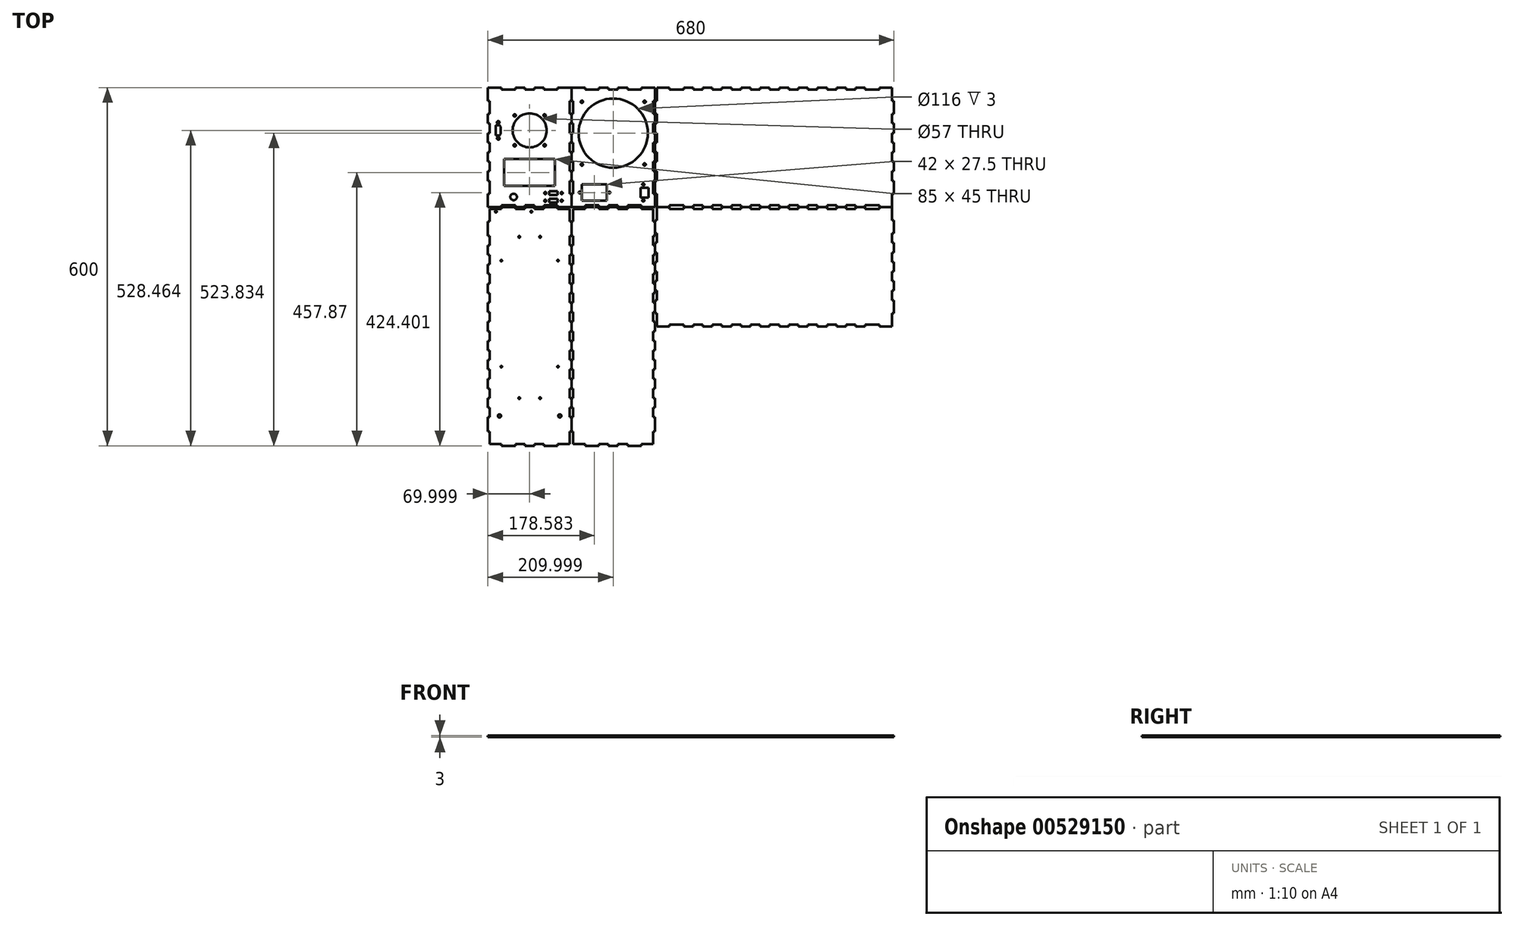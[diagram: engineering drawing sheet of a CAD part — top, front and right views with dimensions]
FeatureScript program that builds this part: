
annotation { "Feature Type Name" : "Feature", "Feature Type Description" : "" }
export const myFeature = defineFeature(function(context is Context, id is Id, definition is map)
    precondition{}
    {
        {
            var Q0;
            Q0=qCreatedBy(makeId("Top.planeOp"),FACE);
            var sketch = newSketch(context, id + "F0", { "sketchPlane" : qUnion([Q0])});
            skLineSegment(sketch, "E0", {"start": v(-340, 300) * mm, "end": v(-317, 300) * mm});
            skLineSegment(sketch, "E1", {"start": v(-317, 300) * mm, "end": v(-317, 297) * mm});
            skLineSegment(sketch, "E2", {"start": v(-317, 297) * mm, "end": v(-294, 297) * mm});
            skLineSegment(sketch, "E3", {"start": v(-294, 297) * mm, "end": v(-294, 300) * mm});
            skLineSegment(sketch, "E4", {"start": v(-294, 300) * mm, "end": v(-278, 300) * mm});
            skLineSegment(sketch, "E5", {"start": v(-278, 300) * mm, "end": v(-278, 297) * mm});
            skLineSegment(sketch, "E6", {"start": v(-278, 297) * mm, "end": v(-262, 297) * mm});
            skLineSegment(sketch, "E7", {"start": v(-262, 297) * mm, "end": v(-262, 300) * mm});
            skLineSegment(sketch, "E8", {"start": v(-262, 300) * mm, "end": v(-246, 300) * mm});
            skLineSegment(sketch, "E9", {"start": v(-246, 300) * mm, "end": v(-246, 297) * mm});
            skLineSegment(sketch, "E10", {"start": v(-246, 297) * mm, "end": v(-223, 297) * mm});
            skLineSegment(sketch, "E11", {"start": v(-223, 297) * mm, "end": v(-223, 300) * mm});
            skLineSegment(sketch, "E12", {"start": v(-223, 300) * mm, "end": v(-200, 300) * mm});
            skLineSegment(sketch, "E13", {"start": v(-200, 300) * mm, "end": v(-200, 278) * mm});
            skLineSegment(sketch, "E14", {"start": v(-200, 278) * mm, "end": v(-203, 278) * mm});
            skLineSegment(sketch, "E15", {"start": v(-203, 278) * mm, "end": v(-203, 256) * mm});
            skLineSegment(sketch, "E16", {"start": v(-203, 256) * mm, "end": v(-200, 256) * mm});
            skLineSegment(sketch, "E17", {"start": v(-200, 256) * mm, "end": v(-200, 240) * mm});
            skLineSegment(sketch, "E18", {"start": v(-200, 240) * mm, "end": v(-203, 240) * mm});
            skLineSegment(sketch, "E19", {"start": v(-203, 240) * mm, "end": v(-203, 224) * mm});
            skLineSegment(sketch, "E20", {"start": v(-203, 224) * mm, "end": v(-200, 224) * mm});
            skLineSegment(sketch, "E21", {"start": v(-200, 224) * mm, "end": v(-200, 208) * mm});
            skLineSegment(sketch, "E22", {"start": v(-200, 208) * mm, "end": v(-203, 208) * mm});
            skLineSegment(sketch, "E23", {"start": v(-203, 208) * mm, "end": v(-203, 192) * mm});
            skLineSegment(sketch, "E24", {"start": v(-203, 192) * mm, "end": v(-200, 192) * mm});
            skLineSegment(sketch, "E25", {"start": v(-200, 192) * mm, "end": v(-200, 176) * mm});
            skLineSegment(sketch, "E26", {"start": v(-200, 176) * mm, "end": v(-203, 176) * mm});
            skLineSegment(sketch, "E27", {"start": v(-203, 176) * mm, "end": v(-203, 160) * mm});
            skLineSegment(sketch, "E28", {"start": v(-203, 160) * mm, "end": v(-200, 160) * mm});
            skLineSegment(sketch, "E29", {"start": v(-200, 160) * mm, "end": v(-200, 144) * mm});
            skLineSegment(sketch, "E30", {"start": v(-200, 144) * mm, "end": v(-203, 144) * mm});
            skLineSegment(sketch, "E31", {"start": v(-203, 144) * mm, "end": v(-203, 122) * mm});
            skLineSegment(sketch, "E32", {"start": v(-203, 122) * mm, "end": v(-200, 122) * mm});
            skLineSegment(sketch, "E33", {"start": v(-200, 122) * mm, "end": v(-200, 100) * mm});
            skLineSegment(sketch, "E34", {"start": v(-200, 100) * mm, "end": v(-223, 100) * mm});
            skLineSegment(sketch, "E35", {"start": v(-223, 100) * mm, "end": v(-223, 103) * mm});
            skLineSegment(sketch, "E36", {"start": v(-223, 103) * mm, "end": v(-246, 103) * mm});
            skLineSegment(sketch, "E37", {"start": v(-246, 103) * mm, "end": v(-246, 100) * mm});
            skLineSegment(sketch, "E38", {"start": v(-246, 100) * mm, "end": v(-262, 100) * mm});
            skLineSegment(sketch, "E39", {"start": v(-262, 100) * mm, "end": v(-262, 103) * mm});
            skLineSegment(sketch, "E40", {"start": v(-262, 103) * mm, "end": v(-278, 103) * mm});
            skLineSegment(sketch, "E41", {"start": v(-278, 103) * mm, "end": v(-278, 100) * mm});
            skLineSegment(sketch, "E42", {"start": v(-278, 100) * mm, "end": v(-294, 100) * mm});
            skLineSegment(sketch, "E43", {"start": v(-294, 100) * mm, "end": v(-294, 103) * mm});
            skLineSegment(sketch, "E44", {"start": v(-294, 103) * mm, "end": v(-317, 103) * mm});
            skLineSegment(sketch, "E45", {"start": v(-317, 103) * mm, "end": v(-317, 100) * mm});
            skLineSegment(sketch, "E46", {"start": v(-317, 100) * mm, "end": v(-340, 100) * mm});
            skLineSegment(sketch, "E47", {"start": v(-340, 100) * mm, "end": v(-340, 122) * mm});
            skLineSegment(sketch, "E48", {"start": v(-340, 122) * mm, "end": v(-337, 122) * mm});
            skLineSegment(sketch, "E49", {"start": v(-337, 122) * mm, "end": v(-337, 144) * mm});
            skLineSegment(sketch, "E50", {"start": v(-337, 144) * mm, "end": v(-340, 144) * mm});
            skLineSegment(sketch, "E51", {"start": v(-340, 144) * mm, "end": v(-340, 160) * mm});
            skLineSegment(sketch, "E52", {"start": v(-340, 160) * mm, "end": v(-337, 160) * mm});
            skLineSegment(sketch, "E53", {"start": v(-337, 160) * mm, "end": v(-337, 176) * mm});
            skLineSegment(sketch, "E54", {"start": v(-337, 176) * mm, "end": v(-340, 176) * mm});
            skLineSegment(sketch, "E55", {"start": v(-340, 176) * mm, "end": v(-340, 192) * mm});
            skLineSegment(sketch, "E56", {"start": v(-340, 192) * mm, "end": v(-337, 192) * mm});
            skLineSegment(sketch, "E57", {"start": v(-337, 192) * mm, "end": v(-337, 208) * mm});
            skLineSegment(sketch, "E58", {"start": v(-337, 208) * mm, "end": v(-340, 208) * mm});
            skLineSegment(sketch, "E59", {"start": v(-340, 208) * mm, "end": v(-340, 224) * mm});
            skLineSegment(sketch, "E60", {"start": v(-340, 224) * mm, "end": v(-337, 224) * mm});
            skLineSegment(sketch, "E61", {"start": v(-337, 224) * mm, "end": v(-337, 240) * mm});
            skLineSegment(sketch, "E62", {"start": v(-337, 240) * mm, "end": v(-340, 240) * mm});
            skLineSegment(sketch, "E63", {"start": v(-340, 240) * mm, "end": v(-340, 256) * mm});
            skLineSegment(sketch, "E64", {"start": v(-340, 256) * mm, "end": v(-337, 256) * mm});
            skLineSegment(sketch, "E65", {"start": v(-337, 256) * mm, "end": v(-337, 278) * mm});
            skLineSegment(sketch, "E66", {"start": v(-337, 278) * mm, "end": v(-340, 278) * mm});
            skLineSegment(sketch, "E67", {"start": v(-340, 278) * mm, "end": v(-340, 300) * mm});
            skLineSegment(sketch, "E68", {"start": v(-200, 300) * mm, "end": v(-177, 300) * mm});
            skLineSegment(sketch, "E69", {"start": v(-177, 300) * mm, "end": v(-177, 297) * mm});
            skLineSegment(sketch, "E70", {"start": v(-177, 297) * mm, "end": v(-154, 297) * mm});
            skLineSegment(sketch, "E71", {"start": v(-154, 297) * mm, "end": v(-154, 300) * mm});
            skLineSegment(sketch, "E72", {"start": v(-154, 300) * mm, "end": v(-138, 300) * mm});
            skLineSegment(sketch, "E73", {"start": v(-138, 300) * mm, "end": v(-138, 297) * mm});
            skLineSegment(sketch, "E74", {"start": v(-138, 297) * mm, "end": v(-122, 297) * mm});
            skLineSegment(sketch, "E75", {"start": v(-122, 297) * mm, "end": v(-122, 300) * mm});
            skLineSegment(sketch, "E76", {"start": v(-122, 300) * mm, "end": v(-106, 300) * mm});
            skLineSegment(sketch, "E77", {"start": v(-106, 300) * mm, "end": v(-106, 297) * mm});
            skLineSegment(sketch, "E78", {"start": v(-106, 297) * mm, "end": v(-83, 297) * mm});
            skLineSegment(sketch, "E79", {"start": v(-83, 297) * mm, "end": v(-83, 300) * mm});
            skLineSegment(sketch, "E80", {"start": v(-83, 300) * mm, "end": v(-60, 300) * mm});
            skLineSegment(sketch, "E81", {"start": v(-60, 300) * mm, "end": v(-60, 278) * mm});
            skLineSegment(sketch, "E82", {"start": v(-60, 278) * mm, "end": v(-63, 278) * mm});
            skLineSegment(sketch, "E83", {"start": v(-63, 278) * mm, "end": v(-63, 256) * mm});
            skLineSegment(sketch, "E84", {"start": v(-63, 256) * mm, "end": v(-60, 256) * mm});
            skLineSegment(sketch, "E85", {"start": v(-60, 256) * mm, "end": v(-60, 240) * mm});
            skLineSegment(sketch, "E86", {"start": v(-60, 240) * mm, "end": v(-63, 240) * mm});
            skLineSegment(sketch, "E87", {"start": v(-63, 240) * mm, "end": v(-63, 224) * mm});
            skLineSegment(sketch, "E88", {"start": v(-63, 224) * mm, "end": v(-60, 224) * mm});
            skLineSegment(sketch, "E89", {"start": v(-60, 224) * mm, "end": v(-60, 208) * mm});
            skLineSegment(sketch, "E90", {"start": v(-60, 208) * mm, "end": v(-63, 208) * mm});
            skLineSegment(sketch, "E91", {"start": v(-63, 208) * mm, "end": v(-63, 192) * mm});
            skLineSegment(sketch, "E92", {"start": v(-63, 192) * mm, "end": v(-60, 192) * mm});
            skLineSegment(sketch, "E93", {"start": v(-60, 192) * mm, "end": v(-60, 176) * mm});
            skLineSegment(sketch, "E94", {"start": v(-60, 176) * mm, "end": v(-63, 176) * mm});
            skLineSegment(sketch, "E95", {"start": v(-63, 176) * mm, "end": v(-63, 160) * mm});
            skLineSegment(sketch, "E96", {"start": v(-63, 160) * mm, "end": v(-60, 160) * mm});
            skLineSegment(sketch, "E97", {"start": v(-60, 160) * mm, "end": v(-60, 144) * mm});
            skLineSegment(sketch, "E98", {"start": v(-60, 144) * mm, "end": v(-63, 144) * mm});
            skLineSegment(sketch, "E99", {"start": v(-63, 144) * mm, "end": v(-63, 122) * mm});
            skLineSegment(sketch, "E100", {"start": v(-63, 122) * mm, "end": v(-60, 122) * mm});
            skLineSegment(sketch, "E101", {"start": v(-60, 122) * mm, "end": v(-60, 100) * mm});
            skLineSegment(sketch, "E102", {"start": v(-60, 100) * mm, "end": v(-83, 100) * mm});
            skLineSegment(sketch, "E103", {"start": v(-83, 100) * mm, "end": v(-83, 103) * mm});
            skLineSegment(sketch, "E104", {"start": v(-83, 103) * mm, "end": v(-106, 103) * mm});
            skLineSegment(sketch, "E105", {"start": v(-106, 103) * mm, "end": v(-106, 100) * mm});
            skLineSegment(sketch, "E106", {"start": v(-106, 100) * mm, "end": v(-122, 100) * mm});
            skLineSegment(sketch, "E107", {"start": v(-122, 100) * mm, "end": v(-122, 103) * mm});
            skLineSegment(sketch, "E108", {"start": v(-122, 103) * mm, "end": v(-138, 103) * mm});
            skLineSegment(sketch, "E109", {"start": v(-138, 103) * mm, "end": v(-138, 100) * mm});
            skLineSegment(sketch, "E110", {"start": v(-138, 100) * mm, "end": v(-154, 100) * mm});
            skLineSegment(sketch, "E111", {"start": v(-154, 100) * mm, "end": v(-154, 103) * mm});
            skLineSegment(sketch, "E112", {"start": v(-154, 103) * mm, "end": v(-177, 103) * mm});
            skLineSegment(sketch, "E113", {"start": v(-177, 103) * mm, "end": v(-177, 100) * mm});
            skLineSegment(sketch, "E114", {"start": v(-177, 100) * mm, "end": v(-200, 100) * mm});
            skLineSegment(sketch, "E115", {"start": v(-200, 100) * mm, "end": v(-200, 122) * mm});
            skLineSegment(sketch, "E116", {"start": v(-200, 122) * mm, "end": v(-197, 122) * mm});
            skLineSegment(sketch, "E117", {"start": v(-197, 122) * mm, "end": v(-197, 144) * mm});
            skLineSegment(sketch, "E118", {"start": v(-197, 144) * mm, "end": v(-200, 144) * mm});
            skLineSegment(sketch, "E119", {"start": v(-200, 144) * mm, "end": v(-200, 160) * mm});
            skLineSegment(sketch, "E120", {"start": v(-200, 160) * mm, "end": v(-197, 160) * mm});
            skLineSegment(sketch, "E121", {"start": v(-197, 160) * mm, "end": v(-197, 176) * mm});
            skLineSegment(sketch, "E122", {"start": v(-197, 176) * mm, "end": v(-200, 176) * mm});
            skLineSegment(sketch, "E123", {"start": v(-200, 176) * mm, "end": v(-200, 192) * mm});
            skLineSegment(sketch, "E124", {"start": v(-200, 192) * mm, "end": v(-197, 192) * mm});
            skLineSegment(sketch, "E125", {"start": v(-197, 192) * mm, "end": v(-197, 208) * mm});
            skLineSegment(sketch, "E126", {"start": v(-197, 208) * mm, "end": v(-200, 208) * mm});
            skLineSegment(sketch, "E127", {"start": v(-200, 208) * mm, "end": v(-200, 224) * mm});
            skLineSegment(sketch, "E128", {"start": v(-200, 224) * mm, "end": v(-197, 224) * mm});
            skLineSegment(sketch, "E129", {"start": v(-197, 224) * mm, "end": v(-197, 240) * mm});
            skLineSegment(sketch, "E130", {"start": v(-197, 240) * mm, "end": v(-200, 240) * mm});
            skLineSegment(sketch, "E131", {"start": v(-200, 240) * mm, "end": v(-200, 256) * mm});
            skLineSegment(sketch, "E132", {"start": v(-200, 256) * mm, "end": v(-197, 256) * mm});
            skLineSegment(sketch, "E133", {"start": v(-197, 256) * mm, "end": v(-197, 278) * mm});
            skLineSegment(sketch, "E134", {"start": v(-197, 278) * mm, "end": v(-200, 278) * mm});
            skLineSegment(sketch, "E135", {"start": v(-200, 278) * mm, "end": v(-200, 300) * mm});
            skLineSegment(sketch, "E136", {"start": v(-57, 300) * mm, "end": v(-36, 300) * mm});
            skLineSegment(sketch, "E137", {"start": v(-36, 300) * mm, "end": v(-36, 297) * mm});
            skLineSegment(sketch, "E138", {"start": v(-36, 297) * mm, "end": v(-12, 297) * mm});
            skLineSegment(sketch, "E139", {"start": v(-12, 297) * mm, "end": v(-12, 300) * mm});
            skLineSegment(sketch, "E140", {"start": v(-12, 300) * mm, "end": v(4, 300) * mm});
            skLineSegment(sketch, "E141", {"start": v(4, 300) * mm, "end": v(4, 297) * mm});
            skLineSegment(sketch, "E142", {"start": v(4, 297) * mm, "end": v(20, 297) * mm});
            skLineSegment(sketch, "E143", {"start": v(20, 297) * mm, "end": v(20, 300) * mm});
            skLineSegment(sketch, "E144", {"start": v(20, 300) * mm, "end": v(36, 300) * mm});
            skLineSegment(sketch, "E145", {"start": v(36, 300) * mm, "end": v(36, 297) * mm});
            skLineSegment(sketch, "E146", {"start": v(36, 297) * mm, "end": v(52, 297) * mm});
            skLineSegment(sketch, "E147", {"start": v(52, 297) * mm, "end": v(52, 300) * mm});
            skLineSegment(sketch, "E148", {"start": v(52, 300) * mm, "end": v(68, 300) * mm});
            skLineSegment(sketch, "E149", {"start": v(68, 300) * mm, "end": v(68, 297) * mm});
            skLineSegment(sketch, "E150", {"start": v(68, 297) * mm, "end": v(84, 297) * mm});
            skLineSegment(sketch, "E151", {"start": v(84, 297) * mm, "end": v(84, 300) * mm});
            skLineSegment(sketch, "E152", {"start": v(84, 300) * mm, "end": v(100, 300) * mm});
            skLineSegment(sketch, "E153", {"start": v(100, 300) * mm, "end": v(100, 297) * mm});
            skLineSegment(sketch, "E154", {"start": v(100, 297) * mm, "end": v(116, 297) * mm});
            skLineSegment(sketch, "E155", {"start": v(116, 297) * mm, "end": v(116, 300) * mm});
            skLineSegment(sketch, "E156", {"start": v(116, 300) * mm, "end": v(132, 300) * mm});
            skLineSegment(sketch, "E157", {"start": v(132, 300) * mm, "end": v(132, 297) * mm});
            skLineSegment(sketch, "E158", {"start": v(132, 297) * mm, "end": v(148, 297) * mm});
            skLineSegment(sketch, "E159", {"start": v(148, 297) * mm, "end": v(148, 300) * mm});
            skLineSegment(sketch, "E160", {"start": v(148, 300) * mm, "end": v(164, 300) * mm});
            skLineSegment(sketch, "E161", {"start": v(164, 300) * mm, "end": v(164, 297) * mm});
            skLineSegment(sketch, "E162", {"start": v(164, 297) * mm, "end": v(180, 297) * mm});
            skLineSegment(sketch, "E163", {"start": v(180, 297) * mm, "end": v(180, 300) * mm});
            skLineSegment(sketch, "E164", {"start": v(180, 300) * mm, "end": v(196, 300) * mm});
            skLineSegment(sketch, "E165", {"start": v(196, 300) * mm, "end": v(196, 297) * mm});
            skLineSegment(sketch, "E166", {"start": v(196, 297) * mm, "end": v(212, 297) * mm});
            skLineSegment(sketch, "E167", {"start": v(212, 297) * mm, "end": v(212, 300) * mm});
            skLineSegment(sketch, "E168", {"start": v(212, 300) * mm, "end": v(228, 300) * mm});
            skLineSegment(sketch, "E169", {"start": v(228, 300) * mm, "end": v(228, 297) * mm});
            skLineSegment(sketch, "E170", {"start": v(228, 297) * mm, "end": v(244, 297) * mm});
            skLineSegment(sketch, "E171", {"start": v(244, 297) * mm, "end": v(244, 300) * mm});
            skLineSegment(sketch, "E172", {"start": v(244, 300) * mm, "end": v(260, 300) * mm});
            skLineSegment(sketch, "E173", {"start": v(260, 300) * mm, "end": v(260, 297) * mm});
            skLineSegment(sketch, "E174", {"start": v(260, 297) * mm, "end": v(276, 297) * mm});
            skLineSegment(sketch, "E175", {"start": v(276, 297) * mm, "end": v(276, 300) * mm});
            skLineSegment(sketch, "E176", {"start": v(276, 300) * mm, "end": v(292, 300) * mm});
            skLineSegment(sketch, "E177", {"start": v(292, 300) * mm, "end": v(292, 297) * mm});
            skLineSegment(sketch, "E178", {"start": v(292, 297) * mm, "end": v(316, 297) * mm});
            skLineSegment(sketch, "E179", {"start": v(316, 297) * mm, "end": v(316, 300) * mm});
            skLineSegment(sketch, "E180", {"start": v(316, 300) * mm, "end": v(337, 300) * mm});
            skLineSegment(sketch, "E181", {"start": v(337, 300) * mm, "end": v(337, 278) * mm});
            skLineSegment(sketch, "E182", {"start": v(337, 278) * mm, "end": v(340, 278) * mm});
            skLineSegment(sketch, "E183", {"start": v(340, 278) * mm, "end": v(340, 256) * mm});
            skLineSegment(sketch, "E184", {"start": v(340, 256) * mm, "end": v(337, 256) * mm});
            skLineSegment(sketch, "E185", {"start": v(337, 256) * mm, "end": v(337, 240) * mm});
            skLineSegment(sketch, "E186", {"start": v(337, 240) * mm, "end": v(340, 240) * mm});
            skLineSegment(sketch, "E187", {"start": v(340, 240) * mm, "end": v(340, 224) * mm});
            skLineSegment(sketch, "E188", {"start": v(340, 224) * mm, "end": v(337, 224) * mm});
            skLineSegment(sketch, "E189", {"start": v(337, 224) * mm, "end": v(337, 208) * mm});
            skLineSegment(sketch, "E190", {"start": v(337, 208) * mm, "end": v(340, 208) * mm});
            skLineSegment(sketch, "E191", {"start": v(340, 208) * mm, "end": v(340, 192) * mm});
            skLineSegment(sketch, "E192", {"start": v(340, 192) * mm, "end": v(337, 192) * mm});
            skLineSegment(sketch, "E193", {"start": v(337, 192) * mm, "end": v(337, 176) * mm});
            skLineSegment(sketch, "E194", {"start": v(337, 176) * mm, "end": v(340, 176) * mm});
            skLineSegment(sketch, "E195", {"start": v(340, 176) * mm, "end": v(340, 160) * mm});
            skLineSegment(sketch, "E196", {"start": v(340, 160) * mm, "end": v(337, 160) * mm});
            skLineSegment(sketch, "E197", {"start": v(337, 160) * mm, "end": v(337, 144) * mm});
            skLineSegment(sketch, "E198", {"start": v(337, 144) * mm, "end": v(340, 144) * mm});
            skLineSegment(sketch, "E199", {"start": v(340, 144) * mm, "end": v(340, 122) * mm});
            skLineSegment(sketch, "E200", {"start": v(340, 122) * mm, "end": v(337, 122) * mm});
            skLineSegment(sketch, "E201", {"start": v(337, 122) * mm, "end": v(337, 100) * mm});
            skLineSegment(sketch, "E202", {"start": v(337, 100) * mm, "end": v(316, 100) * mm});
            skLineSegment(sketch, "E203", {"start": v(316, 100) * mm, "end": v(316, 103) * mm});
            skLineSegment(sketch, "E204", {"start": v(316, 103) * mm, "end": v(292, 103) * mm});
            skLineSegment(sketch, "E205", {"start": v(292, 103) * mm, "end": v(292, 100) * mm});
            skLineSegment(sketch, "E206", {"start": v(292, 100) * mm, "end": v(276, 100) * mm});
            skLineSegment(sketch, "E207", {"start": v(276, 100) * mm, "end": v(276, 103) * mm});
            skLineSegment(sketch, "E208", {"start": v(276, 103) * mm, "end": v(260, 103) * mm});
            skLineSegment(sketch, "E209", {"start": v(260, 103) * mm, "end": v(260, 100) * mm});
            skLineSegment(sketch, "E210", {"start": v(260, 100) * mm, "end": v(244, 100) * mm});
            skLineSegment(sketch, "E211", {"start": v(244, 100) * mm, "end": v(244, 103) * mm});
            skLineSegment(sketch, "E212", {"start": v(244, 103) * mm, "end": v(228, 103) * mm});
            skLineSegment(sketch, "E213", {"start": v(228, 103) * mm, "end": v(228, 100) * mm});
            skLineSegment(sketch, "E214", {"start": v(228, 100) * mm, "end": v(212, 100) * mm});
            skLineSegment(sketch, "E215", {"start": v(212, 100) * mm, "end": v(212, 103) * mm});
            skLineSegment(sketch, "E216", {"start": v(212, 103) * mm, "end": v(196, 103) * mm});
            skLineSegment(sketch, "E217", {"start": v(196, 103) * mm, "end": v(196, 100) * mm});
            skLineSegment(sketch, "E218", {"start": v(196, 100) * mm, "end": v(180, 100) * mm});
            skLineSegment(sketch, "E219", {"start": v(180, 100) * mm, "end": v(180, 103) * mm});
            skLineSegment(sketch, "E220", {"start": v(180, 103) * mm, "end": v(164, 103) * mm});
            skLineSegment(sketch, "E221", {"start": v(164, 103) * mm, "end": v(164, 100) * mm});
            skLineSegment(sketch, "E222", {"start": v(164, 100) * mm, "end": v(148, 100) * mm});
            skLineSegment(sketch, "E223", {"start": v(148, 100) * mm, "end": v(148, 103) * mm});
            skLineSegment(sketch, "E224", {"start": v(148, 103) * mm, "end": v(132, 103) * mm});
            skLineSegment(sketch, "E225", {"start": v(132, 103) * mm, "end": v(132, 100) * mm});
            skLineSegment(sketch, "E226", {"start": v(132, 100) * mm, "end": v(116, 100) * mm});
            skLineSegment(sketch, "E227", {"start": v(116, 100) * mm, "end": v(116, 103) * mm});
            skLineSegment(sketch, "E228", {"start": v(116, 103) * mm, "end": v(100, 103) * mm});
            skLineSegment(sketch, "E229", {"start": v(100, 103) * mm, "end": v(100, 100) * mm});
            skLineSegment(sketch, "E230", {"start": v(100, 100) * mm, "end": v(84, 100) * mm});
            skLineSegment(sketch, "E231", {"start": v(84, 100) * mm, "end": v(84, 103) * mm});
            skLineSegment(sketch, "E232", {"start": v(84, 103) * mm, "end": v(68, 103) * mm});
            skLineSegment(sketch, "E233", {"start": v(68, 103) * mm, "end": v(68, 100) * mm});
            skLineSegment(sketch, "E234", {"start": v(68, 100) * mm, "end": v(52, 100) * mm});
            skLineSegment(sketch, "E235", {"start": v(52, 100) * mm, "end": v(52, 103) * mm});
            skLineSegment(sketch, "E236", {"start": v(52, 103) * mm, "end": v(36, 103) * mm});
            skLineSegment(sketch, "E237", {"start": v(36, 103) * mm, "end": v(36, 100) * mm});
            skLineSegment(sketch, "E238", {"start": v(36, 100) * mm, "end": v(20, 100) * mm});
            skLineSegment(sketch, "E239", {"start": v(20, 100) * mm, "end": v(20, 103) * mm});
            skLineSegment(sketch, "E240", {"start": v(20, 103) * mm, "end": v(4, 103) * mm});
            skLineSegment(sketch, "E241", {"start": v(4, 103) * mm, "end": v(4, 100) * mm});
            skLineSegment(sketch, "E242", {"start": v(4, 100) * mm, "end": v(-12, 100) * mm});
            skLineSegment(sketch, "E243", {"start": v(-12, 100) * mm, "end": v(-12, 103) * mm});
            skLineSegment(sketch, "E244", {"start": v(-12, 103) * mm, "end": v(-36, 103) * mm});
            skLineSegment(sketch, "E245", {"start": v(-36, 103) * mm, "end": v(-36, 100) * mm});
            skLineSegment(sketch, "E246", {"start": v(-36, 100) * mm, "end": v(-57, 100) * mm});
            skLineSegment(sketch, "E247", {"start": v(-57, 100) * mm, "end": v(-57, 122) * mm});
            skLineSegment(sketch, "E248", {"start": v(-57, 122) * mm, "end": v(-60, 122) * mm});
            skLineSegment(sketch, "E249", {"start": v(-60, 122) * mm, "end": v(-60, 144) * mm});
            skLineSegment(sketch, "E250", {"start": v(-60, 144) * mm, "end": v(-57, 144) * mm});
            skLineSegment(sketch, "E251", {"start": v(-57, 144) * mm, "end": v(-57, 160) * mm});
            skLineSegment(sketch, "E252", {"start": v(-57, 160) * mm, "end": v(-60, 160) * mm});
            skLineSegment(sketch, "E253", {"start": v(-60, 160) * mm, "end": v(-60, 176) * mm});
            skLineSegment(sketch, "E254", {"start": v(-60, 176) * mm, "end": v(-57, 176) * mm});
            skLineSegment(sketch, "E255", {"start": v(-57, 176) * mm, "end": v(-57, 192) * mm});
            skLineSegment(sketch, "E256", {"start": v(-57, 192) * mm, "end": v(-60, 192) * mm});
            skLineSegment(sketch, "E257", {"start": v(-60, 192) * mm, "end": v(-60, 208) * mm});
            skLineSegment(sketch, "E258", {"start": v(-60, 208) * mm, "end": v(-57, 208) * mm});
            skLineSegment(sketch, "E259", {"start": v(-57, 208) * mm, "end": v(-57, 224) * mm});
            skLineSegment(sketch, "E260", {"start": v(-57, 224) * mm, "end": v(-60, 224) * mm});
            skLineSegment(sketch, "E261", {"start": v(-60, 224) * mm, "end": v(-60, 240) * mm});
            skLineSegment(sketch, "E262", {"start": v(-60, 240) * mm, "end": v(-57, 240) * mm});
            skLineSegment(sketch, "E263", {"start": v(-57, 240) * mm, "end": v(-57, 256) * mm});
            skLineSegment(sketch, "E264", {"start": v(-57, 256) * mm, "end": v(-60, 256) * mm});
            skLineSegment(sketch, "E265", {"start": v(-60, 256) * mm, "end": v(-60, 278) * mm});
            skLineSegment(sketch, "E266", {"start": v(-60, 278) * mm, "end": v(-57, 278) * mm});
            skLineSegment(sketch, "E267", {"start": v(-57, 278) * mm, "end": v(-57, 300) * mm});
            skLineSegment(sketch, "E268", {"start": v(-57, 100) * mm, "end": v(-36, 100) * mm});
            skLineSegment(sketch, "E269", {"start": v(-36, 100) * mm, "end": v(-36, 97) * mm});
            skLineSegment(sketch, "E270", {"start": v(-36, 97) * mm, "end": v(-12, 97) * mm});
            skLineSegment(sketch, "E271", {"start": v(-12, 97) * mm, "end": v(-12, 100) * mm});
            skLineSegment(sketch, "E272", {"start": v(-12, 100) * mm, "end": v(4, 100) * mm});
            skLineSegment(sketch, "E273", {"start": v(4, 100) * mm, "end": v(4, 97) * mm});
            skLineSegment(sketch, "E274", {"start": v(4, 97) * mm, "end": v(20, 97) * mm});
            skLineSegment(sketch, "E275", {"start": v(20, 97) * mm, "end": v(20, 100) * mm});
            skLineSegment(sketch, "E276", {"start": v(20, 100) * mm, "end": v(36, 100) * mm});
            skLineSegment(sketch, "E277", {"start": v(36, 100) * mm, "end": v(36, 97) * mm});
            skLineSegment(sketch, "E278", {"start": v(36, 97) * mm, "end": v(52, 97) * mm});
            skLineSegment(sketch, "E279", {"start": v(52, 97) * mm, "end": v(52, 100) * mm});
            skLineSegment(sketch, "E280", {"start": v(52, 100) * mm, "end": v(68, 100) * mm});
            skLineSegment(sketch, "E281", {"start": v(68, 100) * mm, "end": v(68, 97) * mm});
            skLineSegment(sketch, "E282", {"start": v(68, 97) * mm, "end": v(84, 97) * mm});
            skLineSegment(sketch, "E283", {"start": v(84, 97) * mm, "end": v(84, 100) * mm});
            skLineSegment(sketch, "E284", {"start": v(84, 100) * mm, "end": v(100, 100) * mm});
            skLineSegment(sketch, "E285", {"start": v(100, 100) * mm, "end": v(100, 97) * mm});
            skLineSegment(sketch, "E286", {"start": v(100, 97) * mm, "end": v(116, 97) * mm});
            skLineSegment(sketch, "E287", {"start": v(116, 97) * mm, "end": v(116, 100) * mm});
            skLineSegment(sketch, "E288", {"start": v(116, 100) * mm, "end": v(132, 100) * mm});
            skLineSegment(sketch, "E289", {"start": v(132, 100) * mm, "end": v(132, 97) * mm});
            skLineSegment(sketch, "E290", {"start": v(132, 97) * mm, "end": v(148, 97) * mm});
            skLineSegment(sketch, "E291", {"start": v(148, 97) * mm, "end": v(148, 100) * mm});
            skLineSegment(sketch, "E292", {"start": v(148, 100) * mm, "end": v(164, 100) * mm});
            skLineSegment(sketch, "E293", {"start": v(164, 100) * mm, "end": v(164, 97) * mm});
            skLineSegment(sketch, "E294", {"start": v(164, 97) * mm, "end": v(180, 97) * mm});
            skLineSegment(sketch, "E295", {"start": v(180, 97) * mm, "end": v(180, 100) * mm});
            skLineSegment(sketch, "E296", {"start": v(180, 100) * mm, "end": v(196, 100) * mm});
            skLineSegment(sketch, "E297", {"start": v(196, 100) * mm, "end": v(196, 97) * mm});
            skLineSegment(sketch, "E298", {"start": v(196, 97) * mm, "end": v(212, 97) * mm});
            skLineSegment(sketch, "E299", {"start": v(212, 97) * mm, "end": v(212, 100) * mm});
            skLineSegment(sketch, "E300", {"start": v(212, 100) * mm, "end": v(228, 100) * mm});
            skLineSegment(sketch, "E301", {"start": v(228, 100) * mm, "end": v(228, 97) * mm});
            skLineSegment(sketch, "E302", {"start": v(228, 97) * mm, "end": v(244, 97) * mm});
            skLineSegment(sketch, "E303", {"start": v(244, 97) * mm, "end": v(244, 100) * mm});
            skLineSegment(sketch, "E304", {"start": v(244, 100) * mm, "end": v(260, 100) * mm});
            skLineSegment(sketch, "E305", {"start": v(260, 100) * mm, "end": v(260, 97) * mm});
            skLineSegment(sketch, "E306", {"start": v(260, 97) * mm, "end": v(276, 97) * mm});
            skLineSegment(sketch, "E307", {"start": v(276, 97) * mm, "end": v(276, 100) * mm});
            skLineSegment(sketch, "E308", {"start": v(276, 100) * mm, "end": v(292, 100) * mm});
            skLineSegment(sketch, "E309", {"start": v(292, 100) * mm, "end": v(292, 97) * mm});
            skLineSegment(sketch, "E310", {"start": v(292, 97) * mm, "end": v(316, 97) * mm});
            skLineSegment(sketch, "E311", {"start": v(316, 97) * mm, "end": v(316, 100) * mm});
            skLineSegment(sketch, "E312", {"start": v(316, 100) * mm, "end": v(337, 100) * mm});
            skLineSegment(sketch, "E313", {"start": v(337, 100) * mm, "end": v(337, 78) * mm});
            skLineSegment(sketch, "E314", {"start": v(337, 78) * mm, "end": v(340, 78) * mm});
            skLineSegment(sketch, "E315", {"start": v(340, 78) * mm, "end": v(340, 56) * mm});
            skLineSegment(sketch, "E316", {"start": v(340, 56) * mm, "end": v(337, 56) * mm});
            skLineSegment(sketch, "E317", {"start": v(337, 56) * mm, "end": v(337, 40) * mm});
            skLineSegment(sketch, "E318", {"start": v(337, 40) * mm, "end": v(340, 40) * mm});
            skLineSegment(sketch, "E319", {"start": v(340, 40) * mm, "end": v(340, 24) * mm});
            skLineSegment(sketch, "E320", {"start": v(340, 24) * mm, "end": v(337, 24) * mm});
            skLineSegment(sketch, "E321", {"start": v(337, 24) * mm, "end": v(337, 8) * mm});
            skLineSegment(sketch, "E322", {"start": v(337, 8) * mm, "end": v(340, 8) * mm});
            skLineSegment(sketch, "E323", {"start": v(340, 8) * mm, "end": v(340, -8) * mm});
            skLineSegment(sketch, "E324", {"start": v(340, -8) * mm, "end": v(337, -8) * mm});
            skLineSegment(sketch, "E325", {"start": v(337, -8) * mm, "end": v(337, -24) * mm});
            skLineSegment(sketch, "E326", {"start": v(337, -24) * mm, "end": v(340, -24) * mm});
            skLineSegment(sketch, "E327", {"start": v(340, -24) * mm, "end": v(340, -40) * mm});
            skLineSegment(sketch, "E328", {"start": v(340, -40) * mm, "end": v(337, -40) * mm});
            skLineSegment(sketch, "E329", {"start": v(337, -40) * mm, "end": v(337, -56) * mm});
            skLineSegment(sketch, "E330", {"start": v(337, -56) * mm, "end": v(340, -56) * mm});
            skLineSegment(sketch, "E331", {"start": v(340, -56) * mm, "end": v(340, -78) * mm});
            skLineSegment(sketch, "E332", {"start": v(340, -78) * mm, "end": v(337, -78) * mm});
            skLineSegment(sketch, "E333", {"start": v(337, -78) * mm, "end": v(337, -100) * mm});
            skLineSegment(sketch, "E334", {"start": v(337, -100) * mm, "end": v(316, -100) * mm});
            skLineSegment(sketch, "E335", {"start": v(316, -100) * mm, "end": v(316, -97) * mm});
            skLineSegment(sketch, "E336", {"start": v(316, -97) * mm, "end": v(292, -97) * mm});
            skLineSegment(sketch, "E337", {"start": v(292, -97) * mm, "end": v(292, -100) * mm});
            skLineSegment(sketch, "E338", {"start": v(292, -100) * mm, "end": v(276, -100) * mm});
            skLineSegment(sketch, "E339", {"start": v(276, -100) * mm, "end": v(276, -97) * mm});
            skLineSegment(sketch, "E340", {"start": v(276, -97) * mm, "end": v(260, -97) * mm});
            skLineSegment(sketch, "E341", {"start": v(260, -97) * mm, "end": v(260, -100) * mm});
            skLineSegment(sketch, "E342", {"start": v(260, -100) * mm, "end": v(244, -100) * mm});
            skLineSegment(sketch, "E343", {"start": v(244, -100) * mm, "end": v(244, -97) * mm});
            skLineSegment(sketch, "E344", {"start": v(244, -97) * mm, "end": v(228, -97) * mm});
            skLineSegment(sketch, "E345", {"start": v(228, -97) * mm, "end": v(228, -100) * mm});
            skLineSegment(sketch, "E346", {"start": v(228, -100) * mm, "end": v(212, -100) * mm});
            skLineSegment(sketch, "E347", {"start": v(212, -100) * mm, "end": v(212, -97) * mm});
            skLineSegment(sketch, "E348", {"start": v(212, -97) * mm, "end": v(196, -97) * mm});
            skLineSegment(sketch, "E349", {"start": v(196, -97) * mm, "end": v(196, -100) * mm});
            skLineSegment(sketch, "E350", {"start": v(196, -100) * mm, "end": v(180, -100) * mm});
            skLineSegment(sketch, "E351", {"start": v(180, -100) * mm, "end": v(180, -97) * mm});
            skLineSegment(sketch, "E352", {"start": v(180, -97) * mm, "end": v(164, -97) * mm});
            skLineSegment(sketch, "E353", {"start": v(164, -97) * mm, "end": v(164, -100) * mm});
            skLineSegment(sketch, "E354", {"start": v(164, -100) * mm, "end": v(148, -100) * mm});
            skLineSegment(sketch, "E355", {"start": v(148, -100) * mm, "end": v(148, -97) * mm});
            skLineSegment(sketch, "E356", {"start": v(148, -97) * mm, "end": v(132, -97) * mm});
            skLineSegment(sketch, "E357", {"start": v(132, -97) * mm, "end": v(132, -100) * mm});
            skLineSegment(sketch, "E358", {"start": v(132, -100) * mm, "end": v(116, -100) * mm});
            skLineSegment(sketch, "E359", {"start": v(116, -100) * mm, "end": v(116, -97) * mm});
            skLineSegment(sketch, "E360", {"start": v(116, -97) * mm, "end": v(100, -97) * mm});
            skLineSegment(sketch, "E361", {"start": v(100, -97) * mm, "end": v(100, -100) * mm});
            skLineSegment(sketch, "E362", {"start": v(100, -100) * mm, "end": v(84, -100) * mm});
            skLineSegment(sketch, "E363", {"start": v(84, -100) * mm, "end": v(84, -97) * mm});
            skLineSegment(sketch, "E364", {"start": v(84, -97) * mm, "end": v(68, -97) * mm});
            skLineSegment(sketch, "E365", {"start": v(68, -97) * mm, "end": v(68, -100) * mm});
            skLineSegment(sketch, "E366", {"start": v(68, -100) * mm, "end": v(52, -100) * mm});
            skLineSegment(sketch, "E367", {"start": v(52, -100) * mm, "end": v(52, -97) * mm});
            skLineSegment(sketch, "E368", {"start": v(52, -97) * mm, "end": v(36, -97) * mm});
            skLineSegment(sketch, "E369", {"start": v(36, -97) * mm, "end": v(36, -100) * mm});
            skLineSegment(sketch, "E370", {"start": v(36, -100) * mm, "end": v(20, -100) * mm});
            skLineSegment(sketch, "E371", {"start": v(20, -100) * mm, "end": v(20, -97) * mm});
            skLineSegment(sketch, "E372", {"start": v(20, -97) * mm, "end": v(4, -97) * mm});
            skLineSegment(sketch, "E373", {"start": v(4, -97) * mm, "end": v(4, -100) * mm});
            skLineSegment(sketch, "E374", {"start": v(4, -100) * mm, "end": v(-12, -100) * mm});
            skLineSegment(sketch, "E375", {"start": v(-12, -100) * mm, "end": v(-12, -97) * mm});
            skLineSegment(sketch, "E376", {"start": v(-12, -97) * mm, "end": v(-36, -97) * mm});
            skLineSegment(sketch, "E377", {"start": v(-36, -97) * mm, "end": v(-36, -100) * mm});
            skLineSegment(sketch, "E378", {"start": v(-36, -100) * mm, "end": v(-57, -100) * mm});
            skLineSegment(sketch, "E379", {"start": v(-57, -100) * mm, "end": v(-57, -78) * mm});
            skLineSegment(sketch, "E380", {"start": v(-57, -78) * mm, "end": v(-60, -78) * mm});
            skLineSegment(sketch, "E381", {"start": v(-60, -78) * mm, "end": v(-60, -56) * mm});
            skLineSegment(sketch, "E382", {"start": v(-60, -56) * mm, "end": v(-57, -56) * mm});
            skLineSegment(sketch, "E383", {"start": v(-57, -56) * mm, "end": v(-57, -40) * mm});
            skLineSegment(sketch, "E384", {"start": v(-57, -40) * mm, "end": v(-60, -40) * mm});
            skLineSegment(sketch, "E385", {"start": v(-60, -40) * mm, "end": v(-60, -24) * mm});
            skLineSegment(sketch, "E386", {"start": v(-60, -24) * mm, "end": v(-57, -24) * mm});
            skLineSegment(sketch, "E387", {"start": v(-57, -24) * mm, "end": v(-57, -8) * mm});
            skLineSegment(sketch, "E388", {"start": v(-57, -8) * mm, "end": v(-60, -8) * mm});
            skLineSegment(sketch, "E389", {"start": v(-60, -8) * mm, "end": v(-60, 8) * mm});
            skLineSegment(sketch, "E390", {"start": v(-60, 8) * mm, "end": v(-57, 8) * mm});
            skLineSegment(sketch, "E391", {"start": v(-57, 8) * mm, "end": v(-57, 24) * mm});
            skLineSegment(sketch, "E392", {"start": v(-57, 24) * mm, "end": v(-60, 24) * mm});
            skLineSegment(sketch, "E393", {"start": v(-60, 24) * mm, "end": v(-60, 40) * mm});
            skLineSegment(sketch, "E394", {"start": v(-60, 40) * mm, "end": v(-57, 40) * mm});
            skLineSegment(sketch, "E395", {"start": v(-57, 40) * mm, "end": v(-57, 56) * mm});
            skLineSegment(sketch, "E396", {"start": v(-57, 56) * mm, "end": v(-60, 56) * mm});
            skLineSegment(sketch, "E397", {"start": v(-60, 56) * mm, "end": v(-60, 78) * mm});
            skLineSegment(sketch, "E398", {"start": v(-60, 78) * mm, "end": v(-57, 78) * mm});
            skLineSegment(sketch, "E399", {"start": v(-57, 78) * mm, "end": v(-57, 100) * mm});
            skLineSegment(sketch, "E400", {"start": v(-337, 97) * mm, "end": v(-317, 97) * mm});
            skLineSegment(sketch, "E401", {"start": v(-317, 97) * mm, "end": v(-317, 100) * mm});
            skLineSegment(sketch, "E402", {"start": v(-317, 100) * mm, "end": v(-294, 100) * mm});
            skLineSegment(sketch, "E403", {"start": v(-294, 100) * mm, "end": v(-294, 97) * mm});
            skLineSegment(sketch, "E404", {"start": v(-294, 97) * mm, "end": v(-278, 97) * mm});
            skLineSegment(sketch, "E405", {"start": v(-278, 97) * mm, "end": v(-278, 100) * mm});
            skLineSegment(sketch, "E406", {"start": v(-278, 100) * mm, "end": v(-262, 100) * mm});
            skLineSegment(sketch, "E407", {"start": v(-262, 100) * mm, "end": v(-262, 97) * mm});
            skLineSegment(sketch, "E408", {"start": v(-262, 97) * mm, "end": v(-246, 97) * mm});
            skLineSegment(sketch, "E409", {"start": v(-246, 97) * mm, "end": v(-246, 100) * mm});
            skLineSegment(sketch, "E410", {"start": v(-246, 100) * mm, "end": v(-223, 100) * mm});
            skLineSegment(sketch, "E411", {"start": v(-223, 100) * mm, "end": v(-223, 97) * mm});
            skLineSegment(sketch, "E412", {"start": v(-223, 97) * mm, "end": v(-203, 97) * mm});
            skLineSegment(sketch, "E413", {"start": v(-203, 97) * mm, "end": v(-203, 76) * mm});
            skLineSegment(sketch, "E414", {"start": v(-203, 76) * mm, "end": v(-200, 76) * mm});
            skLineSegment(sketch, "E415", {"start": v(-200, 76) * mm, "end": v(-200, 52) * mm});
            skLineSegment(sketch, "E416", {"start": v(-200, 52) * mm, "end": v(-203, 52) * mm});
            skLineSegment(sketch, "E417", {"start": v(-203, 52) * mm, "end": v(-203, 36) * mm});
            skLineSegment(sketch, "E418", {"start": v(-203, 36) * mm, "end": v(-200, 36) * mm});
            skLineSegment(sketch, "E419", {"start": v(-200, 36) * mm, "end": v(-200, 20) * mm});
            skLineSegment(sketch, "E420", {"start": v(-200, 20) * mm, "end": v(-203, 20) * mm});
            skLineSegment(sketch, "E421", {"start": v(-203, 20) * mm, "end": v(-203, 4) * mm});
            skLineSegment(sketch, "E422", {"start": v(-203, 4) * mm, "end": v(-200, 4) * mm});
            skLineSegment(sketch, "E423", {"start": v(-200, 4) * mm, "end": v(-200, -12) * mm});
            skLineSegment(sketch, "E424", {"start": v(-200, -12) * mm, "end": v(-203, -12) * mm});
            skLineSegment(sketch, "E425", {"start": v(-203, -12) * mm, "end": v(-203, -28) * mm});
            skLineSegment(sketch, "E426", {"start": v(-203, -28) * mm, "end": v(-200, -28) * mm});
            skLineSegment(sketch, "E427", {"start": v(-200, -28) * mm, "end": v(-200, -44) * mm});
            skLineSegment(sketch, "E428", {"start": v(-200, -44) * mm, "end": v(-203, -44) * mm});
            skLineSegment(sketch, "E429", {"start": v(-203, -44) * mm, "end": v(-203, -60) * mm});
            skLineSegment(sketch, "E430", {"start": v(-203, -60) * mm, "end": v(-200, -60) * mm});
            skLineSegment(sketch, "E431", {"start": v(-200, -60) * mm, "end": v(-200, -76) * mm});
            skLineSegment(sketch, "E432", {"start": v(-200, -76) * mm, "end": v(-203, -76) * mm});
            skLineSegment(sketch, "E433", {"start": v(-203, -76) * mm, "end": v(-203, -92) * mm});
            skLineSegment(sketch, "E434", {"start": v(-203, -92) * mm, "end": v(-200, -92) * mm});
            skLineSegment(sketch, "E435", {"start": v(-200, -92) * mm, "end": v(-200, -108) * mm});
            skLineSegment(sketch, "E436", {"start": v(-200, -108) * mm, "end": v(-203, -108) * mm});
            skLineSegment(sketch, "E437", {"start": v(-203, -108) * mm, "end": v(-203, -124) * mm});
            skLineSegment(sketch, "E438", {"start": v(-203, -124) * mm, "end": v(-200, -124) * mm});
            skLineSegment(sketch, "E439", {"start": v(-200, -124) * mm, "end": v(-200, -140) * mm});
            skLineSegment(sketch, "E440", {"start": v(-200, -140) * mm, "end": v(-203, -140) * mm});
            skLineSegment(sketch, "E441", {"start": v(-203, -140) * mm, "end": v(-203, -156) * mm});
            skLineSegment(sketch, "E442", {"start": v(-203, -156) * mm, "end": v(-200, -156) * mm});
            skLineSegment(sketch, "E443", {"start": v(-200, -156) * mm, "end": v(-200, -172) * mm});
            skLineSegment(sketch, "E444", {"start": v(-200, -172) * mm, "end": v(-203, -172) * mm});
            skLineSegment(sketch, "E445", {"start": v(-203, -172) * mm, "end": v(-203, -188) * mm});
            skLineSegment(sketch, "E446", {"start": v(-203, -188) * mm, "end": v(-200, -188) * mm});
            skLineSegment(sketch, "E447", {"start": v(-200, -188) * mm, "end": v(-200, -204) * mm});
            skLineSegment(sketch, "E448", {"start": v(-200, -204) * mm, "end": v(-203, -204) * mm});
            skLineSegment(sketch, "E449", {"start": v(-203, -204) * mm, "end": v(-203, -220) * mm});
            skLineSegment(sketch, "E450", {"start": v(-203, -220) * mm, "end": v(-200, -220) * mm});
            skLineSegment(sketch, "E451", {"start": v(-200, -220) * mm, "end": v(-200, -236) * mm});
            skLineSegment(sketch, "E452", {"start": v(-200, -236) * mm, "end": v(-203, -236) * mm});
            skLineSegment(sketch, "E453", {"start": v(-203, -236) * mm, "end": v(-203, -252) * mm});
            skLineSegment(sketch, "E454", {"start": v(-203, -252) * mm, "end": v(-200, -252) * mm});
            skLineSegment(sketch, "E455", {"start": v(-200, -252) * mm, "end": v(-200, -276) * mm});
            skLineSegment(sketch, "E456", {"start": v(-200, -276) * mm, "end": v(-203, -276) * mm});
            skLineSegment(sketch, "E457", {"start": v(-203, -276) * mm, "end": v(-203, -297) * mm});
            skLineSegment(sketch, "E458", {"start": v(-203, -297) * mm, "end": v(-223, -297) * mm});
            skLineSegment(sketch, "E459", {"start": v(-223, -297) * mm, "end": v(-223, -300) * mm});
            skLineSegment(sketch, "E460", {"start": v(-223, -300) * mm, "end": v(-246, -300) * mm});
            skLineSegment(sketch, "E461", {"start": v(-246, -300) * mm, "end": v(-246, -297) * mm});
            skLineSegment(sketch, "E462", {"start": v(-246, -297) * mm, "end": v(-262, -297) * mm});
            skLineSegment(sketch, "E463", {"start": v(-262, -297) * mm, "end": v(-262, -300) * mm});
            skLineSegment(sketch, "E464", {"start": v(-262, -300) * mm, "end": v(-278, -300) * mm});
            skLineSegment(sketch, "E465", {"start": v(-278, -300) * mm, "end": v(-278, -297) * mm});
            skLineSegment(sketch, "E466", {"start": v(-278, -297) * mm, "end": v(-294, -297) * mm});
            skLineSegment(sketch, "E467", {"start": v(-294, -297) * mm, "end": v(-294, -300) * mm});
            skLineSegment(sketch, "E468", {"start": v(-294, -300) * mm, "end": v(-317, -300) * mm});
            skLineSegment(sketch, "E469", {"start": v(-317, -300) * mm, "end": v(-317, -297) * mm});
            skLineSegment(sketch, "E470", {"start": v(-317, -297) * mm, "end": v(-337, -297) * mm});
            skLineSegment(sketch, "E471", {"start": v(-337, -297) * mm, "end": v(-337, -276) * mm});
            skLineSegment(sketch, "E472", {"start": v(-337, -276) * mm, "end": v(-340, -276) * mm});
            skLineSegment(sketch, "E473", {"start": v(-340, -276) * mm, "end": v(-340, -252) * mm});
            skLineSegment(sketch, "E474", {"start": v(-340, -252) * mm, "end": v(-337, -252) * mm});
            skLineSegment(sketch, "E475", {"start": v(-337, -252) * mm, "end": v(-337, -236) * mm});
            skLineSegment(sketch, "E476", {"start": v(-337, -236) * mm, "end": v(-340, -236) * mm});
            skLineSegment(sketch, "E477", {"start": v(-340, -236) * mm, "end": v(-340, -220) * mm});
            skLineSegment(sketch, "E478", {"start": v(-340, -220) * mm, "end": v(-337, -220) * mm});
            skLineSegment(sketch, "E479", {"start": v(-337, -220) * mm, "end": v(-337, -204) * mm});
            skLineSegment(sketch, "E480", {"start": v(-337, -204) * mm, "end": v(-340, -204) * mm});
            skLineSegment(sketch, "E481", {"start": v(-340, -204) * mm, "end": v(-340, -188) * mm});
            skLineSegment(sketch, "E482", {"start": v(-340, -188) * mm, "end": v(-337, -188) * mm});
            skLineSegment(sketch, "E483", {"start": v(-337, -188) * mm, "end": v(-337, -172) * mm});
            skLineSegment(sketch, "E484", {"start": v(-337, -172) * mm, "end": v(-340, -172) * mm});
            skLineSegment(sketch, "E485", {"start": v(-340, -172) * mm, "end": v(-340, -156) * mm});
            skLineSegment(sketch, "E486", {"start": v(-340, -156) * mm, "end": v(-337, -156) * mm});
            skLineSegment(sketch, "E487", {"start": v(-337, -156) * mm, "end": v(-337, -140) * mm});
            skLineSegment(sketch, "E488", {"start": v(-337, -140) * mm, "end": v(-340, -140) * mm});
            skLineSegment(sketch, "E489", {"start": v(-340, -140) * mm, "end": v(-340, -124) * mm});
            skLineSegment(sketch, "E490", {"start": v(-340, -124) * mm, "end": v(-337, -124) * mm});
            skLineSegment(sketch, "E491", {"start": v(-337, -124) * mm, "end": v(-337, -108) * mm});
            skLineSegment(sketch, "E492", {"start": v(-337, -108) * mm, "end": v(-340, -108) * mm});
            skLineSegment(sketch, "E493", {"start": v(-340, -108) * mm, "end": v(-340, -92) * mm});
            skLineSegment(sketch, "E494", {"start": v(-340, -92) * mm, "end": v(-337, -92) * mm});
            skLineSegment(sketch, "E495", {"start": v(-337, -92) * mm, "end": v(-337, -76) * mm});
            skLineSegment(sketch, "E496", {"start": v(-337, -76) * mm, "end": v(-340, -76) * mm});
            skLineSegment(sketch, "E497", {"start": v(-340, -76) * mm, "end": v(-340, -60) * mm});
            skLineSegment(sketch, "E498", {"start": v(-340, -60) * mm, "end": v(-337, -60) * mm});
            skLineSegment(sketch, "E499", {"start": v(-337, -60) * mm, "end": v(-337, -44) * mm});
            skLineSegment(sketch, "E500", {"start": v(-337, -44) * mm, "end": v(-340, -44) * mm});
            skLineSegment(sketch, "E501", {"start": v(-340, -44) * mm, "end": v(-340, -28) * mm});
            skLineSegment(sketch, "E502", {"start": v(-340, -28) * mm, "end": v(-337, -28) * mm});
            skLineSegment(sketch, "E503", {"start": v(-337, -28) * mm, "end": v(-337, -12) * mm});
            skLineSegment(sketch, "E504", {"start": v(-337, -12) * mm, "end": v(-340, -12) * mm});
            skLineSegment(sketch, "E505", {"start": v(-340, -12) * mm, "end": v(-340, 4) * mm});
            skLineSegment(sketch, "E506", {"start": v(-340, 4) * mm, "end": v(-337, 4) * mm});
            skLineSegment(sketch, "E507", {"start": v(-337, 4) * mm, "end": v(-337, 20) * mm});
            skLineSegment(sketch, "E508", {"start": v(-337, 20) * mm, "end": v(-340, 20) * mm});
            skLineSegment(sketch, "E509", {"start": v(-340, 20) * mm, "end": v(-340, 36) * mm});
            skLineSegment(sketch, "E510", {"start": v(-340, 36) * mm, "end": v(-337, 36) * mm});
            skLineSegment(sketch, "E511", {"start": v(-337, 36) * mm, "end": v(-337, 52) * mm});
            skLineSegment(sketch, "E512", {"start": v(-337, 52) * mm, "end": v(-340, 52) * mm});
            skLineSegment(sketch, "E513", {"start": v(-340, 52) * mm, "end": v(-340, 76) * mm});
            skLineSegment(sketch, "E514", {"start": v(-340, 76) * mm, "end": v(-337, 76) * mm});
            skLineSegment(sketch, "E515", {"start": v(-337, 76) * mm, "end": v(-337, 97) * mm});
            skLineSegment(sketch, "E516", {"start": v(-197, 97) * mm, "end": v(-177, 97) * mm});
            skLineSegment(sketch, "E517", {"start": v(-177, 97) * mm, "end": v(-177, 100) * mm});
            skLineSegment(sketch, "E518", {"start": v(-177, 100) * mm, "end": v(-154, 100) * mm});
            skLineSegment(sketch, "E519", {"start": v(-154, 100) * mm, "end": v(-154, 97) * mm});
            skLineSegment(sketch, "E520", {"start": v(-154, 97) * mm, "end": v(-138, 97) * mm});
            skLineSegment(sketch, "E521", {"start": v(-138, 97) * mm, "end": v(-138, 100) * mm});
            skLineSegment(sketch, "E522", {"start": v(-138, 100) * mm, "end": v(-122, 100) * mm});
            skLineSegment(sketch, "E523", {"start": v(-122, 100) * mm, "end": v(-122, 97) * mm});
            skLineSegment(sketch, "E524", {"start": v(-122, 97) * mm, "end": v(-106, 97) * mm});
            skLineSegment(sketch, "E525", {"start": v(-106, 97) * mm, "end": v(-106, 100) * mm});
            skLineSegment(sketch, "E526", {"start": v(-106, 100) * mm, "end": v(-83, 100) * mm});
            skLineSegment(sketch, "E527", {"start": v(-83, 100) * mm, "end": v(-83, 97) * mm});
            skLineSegment(sketch, "E528", {"start": v(-83, 97) * mm, "end": v(-63, 97) * mm});
            skLineSegment(sketch, "E529", {"start": v(-63, 97) * mm, "end": v(-63, 76) * mm});
            skLineSegment(sketch, "E530", {"start": v(-63, 76) * mm, "end": v(-60, 76) * mm});
            skLineSegment(sketch, "E531", {"start": v(-60, 76) * mm, "end": v(-60, 52) * mm});
            skLineSegment(sketch, "E532", {"start": v(-60, 52) * mm, "end": v(-63, 52) * mm});
            skLineSegment(sketch, "E533", {"start": v(-63, 52) * mm, "end": v(-63, 36) * mm});
            skLineSegment(sketch, "E534", {"start": v(-63, 36) * mm, "end": v(-60, 36) * mm});
            skLineSegment(sketch, "E535", {"start": v(-60, 36) * mm, "end": v(-60, 20) * mm});
            skLineSegment(sketch, "E536", {"start": v(-60, 20) * mm, "end": v(-63, 20) * mm});
            skLineSegment(sketch, "E537", {"start": v(-63, 20) * mm, "end": v(-63, 4) * mm});
            skLineSegment(sketch, "E538", {"start": v(-63, 4) * mm, "end": v(-60, 4) * mm});
            skLineSegment(sketch, "E539", {"start": v(-60, 4) * mm, "end": v(-60, -12) * mm});
            skLineSegment(sketch, "E540", {"start": v(-60, -12) * mm, "end": v(-63, -12) * mm});
            skLineSegment(sketch, "E541", {"start": v(-63, -12) * mm, "end": v(-63, -28) * mm});
            skLineSegment(sketch, "E542", {"start": v(-63, -28) * mm, "end": v(-60, -28) * mm});
            skLineSegment(sketch, "E543", {"start": v(-60, -28) * mm, "end": v(-60, -44) * mm});
            skLineSegment(sketch, "E544", {"start": v(-60, -44) * mm, "end": v(-63, -44) * mm});
            skLineSegment(sketch, "E545", {"start": v(-63, -44) * mm, "end": v(-63, -60) * mm});
            skLineSegment(sketch, "E546", {"start": v(-63, -60) * mm, "end": v(-60, -60) * mm});
            skLineSegment(sketch, "E547", {"start": v(-60, -60) * mm, "end": v(-60, -76) * mm});
            skLineSegment(sketch, "E548", {"start": v(-60, -76) * mm, "end": v(-63, -76) * mm});
            skLineSegment(sketch, "E549", {"start": v(-63, -76) * mm, "end": v(-63, -92) * mm});
            skLineSegment(sketch, "E550", {"start": v(-63, -92) * mm, "end": v(-60, -92) * mm});
            skLineSegment(sketch, "E551", {"start": v(-60, -92) * mm, "end": v(-60, -108) * mm});
            skLineSegment(sketch, "E552", {"start": v(-60, -108) * mm, "end": v(-63, -108) * mm});
            skLineSegment(sketch, "E553", {"start": v(-63, -108) * mm, "end": v(-63, -124) * mm});
            skLineSegment(sketch, "E554", {"start": v(-63, -124) * mm, "end": v(-60, -124) * mm});
            skLineSegment(sketch, "E555", {"start": v(-60, -124) * mm, "end": v(-60, -140) * mm});
            skLineSegment(sketch, "E556", {"start": v(-60, -140) * mm, "end": v(-63, -140) * mm});
            skLineSegment(sketch, "E557", {"start": v(-63, -140) * mm, "end": v(-63, -156) * mm});
            skLineSegment(sketch, "E558", {"start": v(-63, -156) * mm, "end": v(-60, -156) * mm});
            skLineSegment(sketch, "E559", {"start": v(-60, -156) * mm, "end": v(-60, -172) * mm});
            skLineSegment(sketch, "E560", {"start": v(-60, -172) * mm, "end": v(-63, -172) * mm});
            skLineSegment(sketch, "E561", {"start": v(-63, -172) * mm, "end": v(-63, -188) * mm});
            skLineSegment(sketch, "E562", {"start": v(-63, -188) * mm, "end": v(-60, -188) * mm});
            skLineSegment(sketch, "E563", {"start": v(-60, -188) * mm, "end": v(-60, -204) * mm});
            skLineSegment(sketch, "E564", {"start": v(-60, -204) * mm, "end": v(-63, -204) * mm});
            skLineSegment(sketch, "E565", {"start": v(-63, -204) * mm, "end": v(-63, -220) * mm});
            skLineSegment(sketch, "E566", {"start": v(-63, -220) * mm, "end": v(-60, -220) * mm});
            skLineSegment(sketch, "E567", {"start": v(-60, -220) * mm, "end": v(-60, -236) * mm});
            skLineSegment(sketch, "E568", {"start": v(-60, -236) * mm, "end": v(-63, -236) * mm});
            skLineSegment(sketch, "E569", {"start": v(-63, -236) * mm, "end": v(-63, -252) * mm});
            skLineSegment(sketch, "E570", {"start": v(-63, -252) * mm, "end": v(-60, -252) * mm});
            skLineSegment(sketch, "E571", {"start": v(-60, -252) * mm, "end": v(-60, -276) * mm});
            skLineSegment(sketch, "E572", {"start": v(-60, -276) * mm, "end": v(-63, -276) * mm});
            skLineSegment(sketch, "E573", {"start": v(-63, -276) * mm, "end": v(-63, -297) * mm});
            skLineSegment(sketch, "E574", {"start": v(-63, -297) * mm, "end": v(-83, -297) * mm});
            skLineSegment(sketch, "E575", {"start": v(-83, -297) * mm, "end": v(-83, -300) * mm});
            skLineSegment(sketch, "E576", {"start": v(-83, -300) * mm, "end": v(-106, -300) * mm});
            skLineSegment(sketch, "E577", {"start": v(-106, -300) * mm, "end": v(-106, -297) * mm});
            skLineSegment(sketch, "E578", {"start": v(-106, -297) * mm, "end": v(-122, -297) * mm});
            skLineSegment(sketch, "E579", {"start": v(-122, -297) * mm, "end": v(-122, -300) * mm});
            skLineSegment(sketch, "E580", {"start": v(-122, -300) * mm, "end": v(-138, -300) * mm});
            skLineSegment(sketch, "E581", {"start": v(-138, -300) * mm, "end": v(-138, -297) * mm});
            skLineSegment(sketch, "E582", {"start": v(-138, -297) * mm, "end": v(-154, -297) * mm});
            skLineSegment(sketch, "E583", {"start": v(-154, -297) * mm, "end": v(-154, -300) * mm});
            skLineSegment(sketch, "E584", {"start": v(-154, -300) * mm, "end": v(-177, -300) * mm});
            skLineSegment(sketch, "E585", {"start": v(-177, -300) * mm, "end": v(-177, -297) * mm});
            skLineSegment(sketch, "E586", {"start": v(-177, -297) * mm, "end": v(-197, -297) * mm});
            skLineSegment(sketch, "E587", {"start": v(-197, -297) * mm, "end": v(-197, -276) * mm});
            skLineSegment(sketch, "E588", {"start": v(-197, -276) * mm, "end": v(-200, -276) * mm});
            skLineSegment(sketch, "E589", {"start": v(-200, -276) * mm, "end": v(-200, -252) * mm});
            skLineSegment(sketch, "E590", {"start": v(-200, -252) * mm, "end": v(-197, -252) * mm});
            skLineSegment(sketch, "E591", {"start": v(-197, -252) * mm, "end": v(-197, -236) * mm});
            skLineSegment(sketch, "E592", {"start": v(-197, -236) * mm, "end": v(-200, -236) * mm});
            skLineSegment(sketch, "E593", {"start": v(-200, -236) * mm, "end": v(-200, -220) * mm});
            skLineSegment(sketch, "E594", {"start": v(-200, -220) * mm, "end": v(-197, -220) * mm});
            skLineSegment(sketch, "E595", {"start": v(-197, -220) * mm, "end": v(-197, -204) * mm});
            skLineSegment(sketch, "E596", {"start": v(-197, -204) * mm, "end": v(-200, -204) * mm});
            skLineSegment(sketch, "E597", {"start": v(-200, -204) * mm, "end": v(-200, -188) * mm});
            skLineSegment(sketch, "E598", {"start": v(-200, -188) * mm, "end": v(-197, -188) * mm});
            skLineSegment(sketch, "E599", {"start": v(-197, -188) * mm, "end": v(-197, -172) * mm});
            skLineSegment(sketch, "E600", {"start": v(-197, -172) * mm, "end": v(-200, -172) * mm});
            skLineSegment(sketch, "E601", {"start": v(-200, -172) * mm, "end": v(-200, -156) * mm});
            skLineSegment(sketch, "E602", {"start": v(-200, -156) * mm, "end": v(-197, -156) * mm});
            skLineSegment(sketch, "E603", {"start": v(-197, -156) * mm, "end": v(-197, -140) * mm});
            skLineSegment(sketch, "E604", {"start": v(-197, -140) * mm, "end": v(-200, -140) * mm});
            skLineSegment(sketch, "E605", {"start": v(-200, -140) * mm, "end": v(-200, -124) * mm});
            skLineSegment(sketch, "E606", {"start": v(-200, -124) * mm, "end": v(-197, -124) * mm});
            skLineSegment(sketch, "E607", {"start": v(-197, -124) * mm, "end": v(-197, -108) * mm});
            skLineSegment(sketch, "E608", {"start": v(-197, -108) * mm, "end": v(-200, -108) * mm});
            skLineSegment(sketch, "E609", {"start": v(-200, -108) * mm, "end": v(-200, -92) * mm});
            skLineSegment(sketch, "E610", {"start": v(-200, -92) * mm, "end": v(-197, -92) * mm});
            skLineSegment(sketch, "E611", {"start": v(-197, -92) * mm, "end": v(-197, -76) * mm});
            skLineSegment(sketch, "E612", {"start": v(-197, -76) * mm, "end": v(-200, -76) * mm});
            skLineSegment(sketch, "E613", {"start": v(-200, -76) * mm, "end": v(-200, -60) * mm});
            skLineSegment(sketch, "E614", {"start": v(-200, -60) * mm, "end": v(-197, -60) * mm});
            skLineSegment(sketch, "E615", {"start": v(-197, -60) * mm, "end": v(-197, -44) * mm});
            skLineSegment(sketch, "E616", {"start": v(-197, -44) * mm, "end": v(-200, -44) * mm});
            skLineSegment(sketch, "E617", {"start": v(-200, -44) * mm, "end": v(-200, -28) * mm});
            skLineSegment(sketch, "E618", {"start": v(-200, -28) * mm, "end": v(-197, -28) * mm});
            skLineSegment(sketch, "E619", {"start": v(-197, -28) * mm, "end": v(-197, -12) * mm});
            skLineSegment(sketch, "E620", {"start": v(-197, -12) * mm, "end": v(-200, -12) * mm});
            skLineSegment(sketch, "E621", {"start": v(-200, -12) * mm, "end": v(-200, 4) * mm});
            skLineSegment(sketch, "E622", {"start": v(-200, 4) * mm, "end": v(-197, 4) * mm});
            skLineSegment(sketch, "E623", {"start": v(-197, 4) * mm, "end": v(-197, 20) * mm});
            skLineSegment(sketch, "E624", {"start": v(-197, 20) * mm, "end": v(-200, 20) * mm});
            skLineSegment(sketch, "E625", {"start": v(-200, 20) * mm, "end": v(-200, 36) * mm});
            skLineSegment(sketch, "E626", {"start": v(-200, 36) * mm, "end": v(-197, 36) * mm});
            skLineSegment(sketch, "E627", {"start": v(-197, 36) * mm, "end": v(-197, 52) * mm});
            skLineSegment(sketch, "E628", {"start": v(-197, 52) * mm, "end": v(-200, 52) * mm});
            skLineSegment(sketch, "E629", {"start": v(-200, 52) * mm, "end": v(-200, 76) * mm});
            skLineSegment(sketch, "E630", {"start": v(-200, 76) * mm, "end": v(-197, 76) * mm});
            skLineSegment(sketch, "E631", {"start": v(-197, 76) * mm, "end": v(-197, 97) * mm});
            skLineSegment(sketch, "E632", {"start": v(-355.22, 55) * mm, "end": v(-207.7, 55) * mm, "construction": true});
            skLineSegment(sketch, "E633", {"start": v(-310, 76.34) * mm, "end": v(-310, -269.67) * mm, "construction": true});
            skLineSegment(sketch, "E634", {"start": v(-337, 86.5) * mm, "end": v(-203, 86.5) * mm, "construction": true});
            skLineSegment(sketch, "E635", {"start": v(-270, 86.5) * mm, "end": v(-270, -289.59) * mm, "construction": true});
            skCircle(sketch, "E636.MirrorC", {"center": v(-222.5, 10.22) * mm, "radius": 1.25 * mm});
            skCircle(sketch, "E637.MirrorC", {"center": v(-317.5, 10.22) * mm, "radius": 1.25 * mm});
            skCircle(sketch, "E638.MirrorC", {"center": v(-317.5, -167.28) * mm, "radius": 1.25 * mm});
            skCircle(sketch, "E639.MirrorC", {"center": v(-222.5, -167.28) * mm, "radius": 1.25 * mm});
            skLineSegment(sketch, "E640", {"start": v(-269.98, 61.02) * mm, "end": v(-269.98, -231.74) * mm, "construction": true});
            skCircle(sketch, "E641", {"center": v(-287.48, 50) * mm, "radius": 1.5 * mm});
            skCircle(sketch, "E642.MirrorC", {"center": v(-252.48, 50) * mm, "radius": 1.5 * mm});
            skCircle(sketch, "E643.MirrorC", {"center": v(-287.48, -219.99) * mm, "radius": 1.5 * mm});
            skCircle(sketch, "E644.MirrorC", {"center": v(-252.48, -219.99) * mm, "radius": 1.5 * mm});
            skCircle(sketch, "E645", {"center": v(-267.1, 92.35) * mm, "radius": 1.5 * mm});
            skCircle(sketch, "E646.MirrorC", {"center": v(-326.6, 92.35) * mm, "radius": 1.5 * mm});
            skCircle(sketch, "E647", {"center": v(-320.5, -249.84) * mm, "radius": 2.75 * mm});
            skCircle(sketch, "E648.MirrorC", {"center": v(-219.5, -249.84) * mm, "radius": 2.75 * mm});
            skLineSegment(sketch, "E649", {"start": v(-270, 321.5) * mm, "end": v(-270, 103) * mm, "construction": true});
            skPoint(sketch, "E649.startSnap0", {"position": v(-270, 297) * mm});
            skLineSegment(sketch, "E650.bottom", {"start": v(-227.5, 135.37) * mm, "end": v(-312.5, 135.37) * mm});
            skLineSegment(sketch, "E650.top", {"start": v(-227.5, 180.37) * mm, "end": v(-312.5, 180.37) * mm});
            skLineSegment(sketch, "E650.left", {"start": v(-227.5, 135.37) * mm, "end": v(-227.5, 180.37) * mm});
            skLineSegment(sketch, "E650.right", {"start": v(-312.5, 135.37) * mm, "end": v(-312.5, 180.37) * mm});
            skPoint(sketch, "E650.middle", {"position": v(-270, 157.87) * mm});
            skCircle(sketch, "E651", {"center": v(-296.86, 117) * mm, "radius": 5.5 * mm});
            skPoint(sketch, "E652.middle", {"position": v(-270, 228.46) * mm});
            skPoint(sketch, "E653.startSnap0", {"position": v(-270, 258.46) * mm});
            skCircle(sketch, "E654", {"center": v(-295, 253.46) * mm, "radius": 2 * mm});
            skCircle(sketch, "E655.MirrorC", {"center": v(-245, 253.46) * mm, "radius": 2 * mm});
            skCircle(sketch, "E656.MirrorC", {"center": v(-295, 203.46) * mm, "radius": 2 * mm});
            skCircle(sketch, "E657.MirrorC", {"center": v(-245, 203.46) * mm, "radius": 2 * mm});
            skCircle(sketch, "E658", {"center": v(-270, 228.46) * mm, "radius": 28.5 * mm});
            skCircle(sketch, "E659", {"center": v(-243.8, 123.46) * mm, "radius": 1.75 * mm});
            skCircle(sketch, "E660.MirrorC", {"center": v(-216.3, 123.46) * mm, "radius": 1.75 * mm});
            skLineSegment(sketch, "E661.bottom", {"start": v(-237.06, 120.23) * mm, "end": v(-237.06, 126.73) * mm});
            skLineSegment(sketch, "E661.top", {"start": v(-223.06, 120.23) * mm, "end": v(-223.06, 126.73) * mm});
            skLineSegment(sketch, "E661.left", {"start": v(-237.06, 120.23) * mm, "end": v(-223.06, 120.23) * mm});
            skLineSegment(sketch, "E661.right", {"start": v(-237.06, 126.73) * mm, "end": v(-223.06, 126.73) * mm});
            skCircle(sketch, "E662", {"center": v(-243.8, 110.66) * mm, "radius": 1.75 * mm});
            skCircle(sketch, "E663.MirrorC", {"center": v(-216.3, 110.66) * mm, "radius": 1.75 * mm});
            skLineSegment(sketch, "E664.bottom", {"start": v(-237.06, 107.44) * mm, "end": v(-237.06, 113.94) * mm});
            skLineSegment(sketch, "E664.top", {"start": v(-223.06, 107.44) * mm, "end": v(-223.06, 113.94) * mm});
            skLineSegment(sketch, "E664.left", {"start": v(-237.06, 107.44) * mm, "end": v(-223.06, 107.44) * mm});
            skLineSegment(sketch, "E664.right", {"start": v(-237.06, 113.94) * mm, "end": v(-223.06, 113.94) * mm});
            skLineSegment(sketch, "E665.bottom", {"start": v(-322.45, 247.13) * mm, "end": v(-322.46, 247.13) * mm});
            skLineSegment(sketch, "E665.top", {"start": v(-322.45, 209.83) * mm, "end": v(-322.46, 209.83) * mm});
            skLineSegment(sketch, "E666", {"start": v(-322.46, 247.13) * mm, "end": v(-322.45, 247.13) * mm, "construction": true});
            skCircle(sketch, "E667", {"center": v(-322.46, 241.88) * mm, "radius": 2.2 * mm});
            skCircle(sketch, "E668.MirrorC", {"center": v(-322.46, 215.07) * mm, "radius": 2.2 * mm});
            skLineSegment(sketch, "E669.bottom", {"start": v(-320.18, 219.73) * mm, "end": v(-326.53, 219.73) * mm});
            skLineSegment(sketch, "E669.top", {"start": v(-320.18, 237.23) * mm, "end": v(-326.53, 237.23) * mm});
            skLineSegment(sketch, "E669.left", {"start": v(-318.4, 222.52) * mm, "end": v(-318.4, 234.43) * mm});
            skLineSegment(sketch, "E669.right", {"start": v(-326.53, 219.73) * mm, "end": v(-326.53, 237.23) * mm});
            skLineSegment(sketch, "E670", {"start": v(-320.18, 237.23) * mm, "end": v(-318.4, 234.43) * mm});
            skLineSegment(sketch, "E671.MirrorCS", {"start": v(-320.18, 219.73) * mm, "end": v(-318.4, 222.52) * mm});
            skPoint(sketch, "E672.middle", {"position": v(-130, 223.83) * mm});
            skPoint(sketch, "E673.startSnap0", {"position": v(-130, 283.83) * mm});
            skPoint(sketch, "E674.startSnap0", {"position": v(-190, 223.83) * mm});
            skCircle(sketch, "E675", {"center": v(-182.5, 276.33) * mm, "radius": 2 * mm});
            skCircle(sketch, "E676.MirrorC", {"center": v(-77.5, 276.33) * mm, "radius": 2 * mm});
            skCircle(sketch, "E677.MirrorC", {"center": v(-182.5, 171.33) * mm, "radius": 2 * mm});
            skCircle(sketch, "E678.MirrorC", {"center": v(-77.5, 171.33) * mm, "radius": 2 * mm});
            skCircle(sketch, "E679", {"center": v(-130, 223.83) * mm, "radius": 58 * mm});
            skLineSegment(sketch, "E680", {"start": v(-130, 297) * mm, "end": v(-130, 103) * mm, "construction": true});
            skLineSegment(sketch, "E681.bottom", {"start": v(-140.42, 110.65) * mm, "end": v(-182.42, 110.65) * mm});
            skLineSegment(sketch, "E681.top", {"start": v(-140.42, 138.15) * mm, "end": v(-182.42, 138.15) * mm});
            skLineSegment(sketch, "E681.left", {"start": v(-140.42, 110.65) * mm, "end": v(-140.42, 138.15) * mm});
            skLineSegment(sketch, "E681.right", {"start": v(-182.42, 110.65) * mm, "end": v(-182.42, 138.15) * mm});
            skCircle(sketch, "E682", {"center": v(-186.42, 124.4) * mm, "radius": 1.5 * mm});
            skCircle(sketch, "E683.MirrorC", {"center": v(-136.42, 124.4) * mm, "radius": 1.5 * mm});
            skLineSegment(sketch, "E684.bottom", {"start": v(-84.2, 132.63) * mm, "end": v(-70.7, 132.63) * mm});
            skLineSegment(sketch, "E684.top", {"start": v(-84.2, 116.13) * mm, "end": v(-70.7, 116.13) * mm});
            skLineSegment(sketch, "E684.left", {"start": v(-84.2, 132.63) * mm, "end": v(-84.2, 116.13) * mm});
            skLineSegment(sketch, "E684.right", {"start": v(-70.7, 132.63) * mm, "end": v(-70.7, 116.13) * mm});
            skCircle(sketch, "E685", {"center": v(-79.7, 137.88) * mm, "radius": 1.75 * mm});
            skCircle(sketch, "E686.MirrorC", {"center": v(-79.7, 110.88) * mm, "radius": 1.75 * mm});
            skLineSegment(sketch, "E687", {"start": v(-326.6, 92.35) * mm, "end": v(-267.1, 92.35) * mm, "construction": true});
            skLineSegment(sketch, "E688", {"start": v(-296.86, 92.35) * mm, "end": v(-296.86, 128.9) * mm, "construction": true});
            skSolve(sketch);
        }
        {
            var Q0;
            Q0=makeQuery(id+"F0.imprint","IMPRINT",FACE,{"disambiguationData":[TD([[makeQuery(id+"F0.imprint","IMPRINT",EDGE,{"derivedFrom":sQuery(id+"F0.wireOp",EDGE,"E0")}),-1.0]])]});
            extrude(context, id + "F1", {"entities" : qUnion([Q0]), "depth" : 3 * mm, "offsetDistance" : 25 * mm});
        }
        {
            var Q0;
            Q0=makeQuery(id+"F0.imprint","IMPRINT",FACE,{"disambiguationData":[TD([[makeQuery(id+"F0.imprint","IMPRINT",EDGE,{"derivedFrom":sQuery(id+"F0.wireOp",EDGE,"E400")}),-1.0]])]});
            extrude(context, id + "F2", {"entities" : qUnion([Q0]), "depth" : 3 * mm, "offsetDistance" : 25 * mm});
        }
        {
            var Q0;
            Q0=makeQuery(id+"F0.imprint","IMPRINT",FACE,{"disambiguationData":[TD([[makeQuery(id+"F0.imprint","IMPRINT",EDGE,{"derivedFrom":sQuery(id+"F0.wireOp",EDGE,"E13")}),1.0]])]});
            extrude(context, id + "F3", {"entities" : qUnion([Q0]), "depth" : 3 * mm, "offsetDistance" : 25 * mm});
        }
        {
            var Q0;
            Q0=makeQuery(id+"F0.imprint","IMPRINT",FACE,{"disambiguationData":[TD([[makeQuery(id+"F0.imprint","IMPRINT",EDGE,{"derivedFrom":sQuery(id+"F0.wireOp",EDGE,"E415")}),1.0]])]});
            extrude(context, id + "F4", {"entities" : qUnion([Q0]), "depth" : 3 * mm, "offsetDistance" : 25 * mm});
        }
        {
            var Q0;
            Q0=makeQuery(id+"F0.imprint","IMPRINT",FACE,{"disambiguationData":[TD([[makeQuery(id+"F0.imprint","IMPRINT",EDGE,{"derivedFrom":sQuery(id+"F0.wireOp",EDGE,"E136")}),-1.0]])]});
            extrude(context, id + "F5", {"entities" : qUnion([Q0]), "depth" : 3 * mm, "offsetDistance" : 25 * mm});
        }
        {
            var Q0;
            Q0=makeQuery(id+"F0.imprint","IMPRINT",FACE,{"disambiguationData":[TD([[makeQuery(id+"F0.imprint","IMPRINT",EDGE,{"derivedFrom":sQuery(id+"F0.wireOp",EDGE,"E202")}),1.0]])]});
            extrude(context, id + "F6", {"entities" : qUnion([Q0]), "depth" : 3 * mm, "offsetDistance" : 25 * mm});
        }
    });
